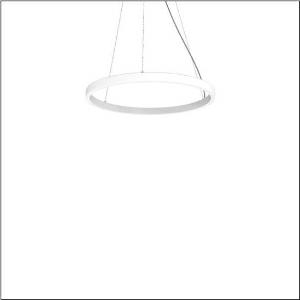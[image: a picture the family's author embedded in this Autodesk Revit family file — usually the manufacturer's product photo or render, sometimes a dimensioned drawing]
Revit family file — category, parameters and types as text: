
# Revit family: silica_21_ring-o_5pjbo2d3004a
name_source: partatom
category: Lighting Fixtures
units: mm (PartAtom-declared; Revit-internal decimal feet)

## family parameters
Cut with Voids When Loaded = No
Host = Face
Light Source = No
Part Type = Normal
Room Calculation Point = No
Round Connector Dimension = Use Diameter
Shared = No

## types (1)
- Silica 21 Ring-O (1 x LED, 4940 lm, 80 W, 4000K)
    Apparent Load = 80 VA
    CIE Flux Codes = 2 16 49 50 100
    Color Rendering = 80
    Color Temperature = 4000K
    Default Elevation = 1800 mm
    Description = Silica 21 Ring-O, suspended luminaire, of PMMA, frosted, light emission: outer ring side luminous distribution, primary light characteristic: symmetric, installation type: suspended mounting, LED, rated luminous flux: 4.940lm, luminous efficacy: 62lm/W, light colour: 840, colour temperature: 4000K, control gear: DALI 2, with terminal, 5-pole, mains connection: 230V, AC/DC, 0/50..60Hz, rated input power: 80W, housing, of extruded aluminium section, traffic white (RAL 9016), diameter: 810mm, ceiling canopy, traffic white (RAL 9016), protection rating (lamp compartment): IP40, insulation class (complete): insulation class I (protective earthing), certification: CE, impact resistance: IK02, permissible operating ambient temperature: 0..+35°C, packaging unit: 1 piece
    Height = 48 mm  [stored 0.15748 ft]
    Lamp = 1 x LED
    Lamp Light Flux = 4940 lm
    Lamp Power = 80 W
    Lamp count = 1
    Length = 810 mm
    Luminous efficacy = 62 lm/W
    Manufacturer = Siteco
    ModVariant = No
    Model = 5PJBO2D3004A
    Mounting Place = Ceiling
    Mounting Type = Pendant
    Number of Poles = 1
    OnlyDefault = Yes
    Power Factor = 1
    Product Name = Silica 21 Ring-O
    Product group = suspended luminaire
    ProductGroupID = 904
    Protection Class = Protection class I
    Protection Degree = IP 40
    RLX_Detail_Level = 1
    RLX_Emergency_Light_Flux = 0 lm
    RLX_Emergency_Type = 0
    RLX_Emergency_Type_DB = No
    RlxData = <blob elided: 11989 chars, md5=963e8d66>
    Socket = socket
    Standby Power = 0 W
    System Light Flux = 4940 lm
    System Power = 80 W
    Type Comments = Product without accessories
    Type Image = l_1258383.jpg
    URL = http://relux.com
    VarID = ---
    Voltage = 0 V
    Weight = 0.00 kg
    Width = 0 mm  [stored 0 ft]

note: [stored X ft] marks values corroborated as IEEE doubles in the binary element streams (Revit-internal decimal feet)

## geometry (parser evidence)
native form markers: Sweep x10
no freeform markers — native parametric forms only
